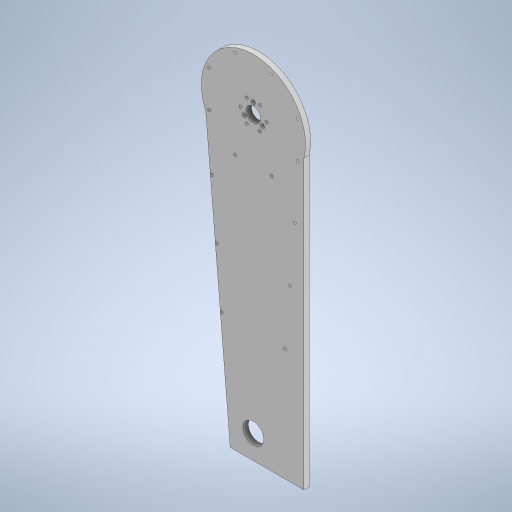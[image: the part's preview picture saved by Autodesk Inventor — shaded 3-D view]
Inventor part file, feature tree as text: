
AUTODESK INVENTOR PART (.ipt)
format: ipt  version: 2024.3 (Build 283343000, 343)  size: 334,848 bytes
history: native  units: mm
features: sketch x7, hole x5, extrude x2, other x1
ambient origin geometry x8: Origin, YZ Plane, XZ Plane, XY Plane, X Axis, Y Axis, Z Axis, Center Point
bodies: Body1 (feature_tree)
feature tree (15):
  other  "ソリッド1"
  extrude  "押し出し1"  Depth=100.0mm
  hole  "穴1"  [1 undecoded]
  extrude  "押し出し3"  Depth=5.0mm TaperAngle=0.0deg
  hole  "穴2"  [1 undecoded]
  hole  "穴3"  [1 undecoded]
  hole  "穴6"  [1 undecoded]
  hole  "穴7"  [1 undecoded]
  sketch  "スケッチ1"
  sketch  "スケッチ2"
  sketch  "スケッチ4"
  sketch  "スケッチ6"
  sketch  "スケッチ7"
  sketch  "スケッチ15"
  sketch  "スケッチ16"
note: 5 required parameter values undecoded (feature->parameter linkage not recoverable at this tier; creation-order binding heuristic only, values carry confidence <= 0.55)
